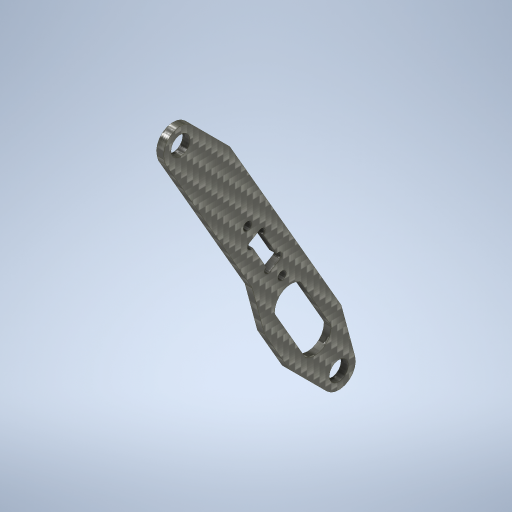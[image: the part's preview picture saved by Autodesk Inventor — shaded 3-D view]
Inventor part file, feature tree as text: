
AUTODESK INVENTOR PART (.ipt)
format: ipt  version: 2024.2 (Build 282272000, 272)  size: 370,176 bytes
history: native  units: mm
features: hole x2, other x1, extrude x1, sketch x1
ambient origin geometry x8: Origin, YZ Plane, XZ Plane, XY Plane, X Axis, Y Axis, Z Axis, Center Point
bodies: Solid1 (feature_tree)
feature tree (5):
  other  "LegLinkBasis.ipt"
  extrude  "Extrusion1"  Depth=3.0mm TaperAngle=0.0deg
  hole  "Phi8.0-H7"  [1 undecoded]
  hole  "Phi3.5"  [1 undecoded]
  sketch  "Sketch1"  dims[d0=10.0mm d1=3.0mm d2=0.0mm d3=8.0mm d4=6.0mm d5=4.0mm d6=2.0mm d7=90.0deg d8=8.0mm d9=20.594885mm d10=3.5mm d11=6.0mm d12=4.0mm d13=2.0mm d14=90.0deg d15=8.0mm d16=20.594885mm d17=2.0mm]
note: 2 required parameter values undecoded (feature->parameter linkage not recoverable at this tier; creation-order binding heuristic only, values carry confidence <= 0.55)
